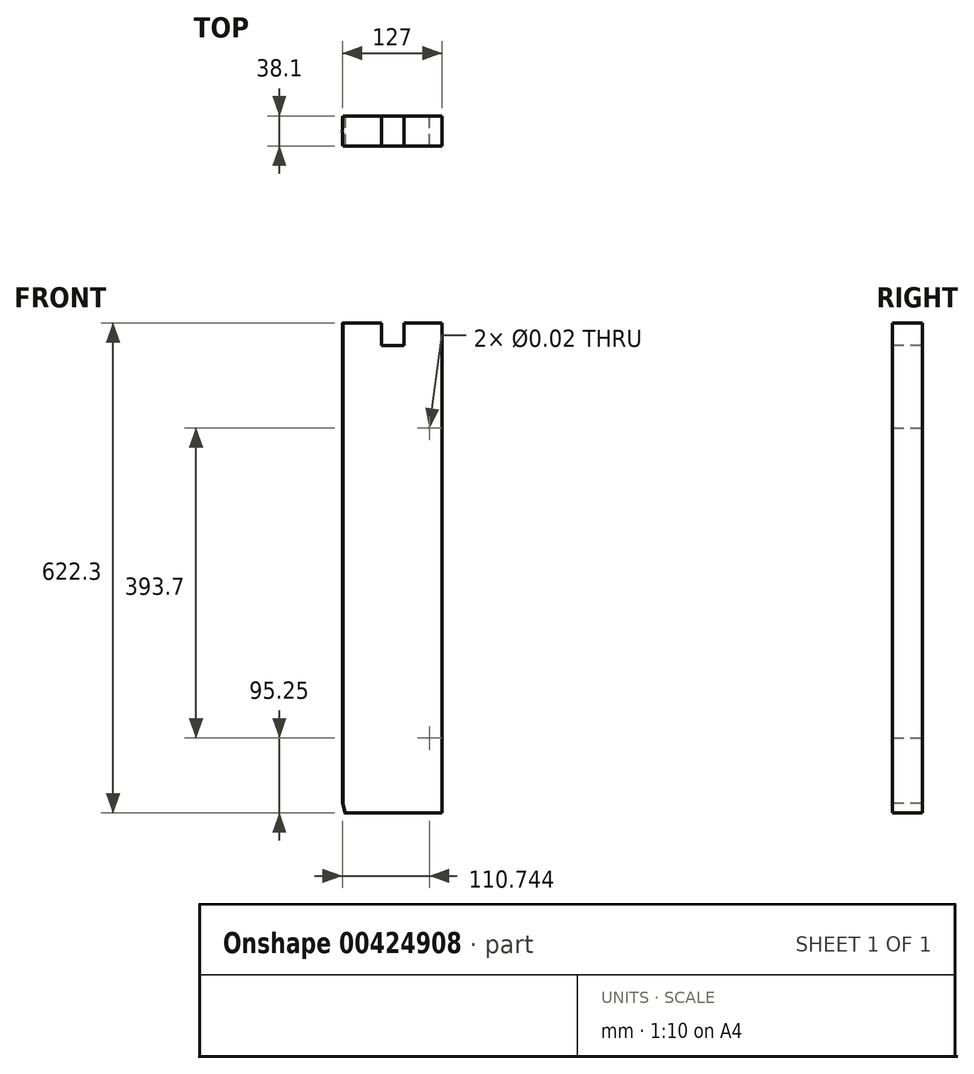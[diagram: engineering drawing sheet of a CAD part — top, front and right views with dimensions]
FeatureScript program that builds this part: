
annotation { "Feature Type Name" : "Feature", "Feature Type Description" : "" }
export const myFeature = defineFeature(function(context is Context, id is Id, definition is map)
    precondition{}
    {
        {
            var Q0;
            Q0=qCreatedBy(makeId("Front.planeOp"),FACE);
            var sketch = newSketch(context, id + "F0", { "sketchPlane" : qUnion([Q0])});
            skLineSegment(sketch, "E0.bottom", {"start": v(63.5, -311.15) * mm, "end": v(-63.5, -311.15) * mm});
            skLineSegment(sketch, "E0.top", {"start": v(63.5, 311.15) * mm, "end": v(-63.5, 311.15) * mm});
            skLineSegment(sketch, "E0.left", {"start": v(63.5, -311.15) * mm, "end": v(63.5, 311.15) * mm});
            skLineSegment(sketch, "E0.right", {"start": v(-63.5, -311.15) * mm, "end": v(-63.5, 311.15) * mm});
            skPoint(sketch, "E0.middle", {"position": v(0, 0) * mm});
            skSolve(sketch);
        }
        {
            var Q0;
            Q0 = qSketchRegion(id + "F0", true);
            extrude(context, id + "F1", {"entities" : qUnion([Q0]), "depth" : 38.1 * mm, "symmetric" : true});
        }
        {
            var Q0;
            Q0=makeQuery(id+"F1.opExtrude","SWEPT_FACE",FACE,{"disambiguationData":[OSD([sQuery(id+"F0.wireOp",EDGE,"E0.top")])]});
            var sketch = newSketch(context, id + "F2", { "sketchPlane" : qUnion([Q0])});
            skLineSegment(sketch, "E1", {"start": v(-63.5, 0) * mm, "end": v(63.5, 0) * mm, "construction": true});
            skCircle(sketch, "E2", {"center": v(186.47, 0) * mm, "radius": 249.97 * mm});
            skLineSegment(sketch, "E3.0", {"start": v(63.5, -19.05) * mm, "end": v(-63.5, -19.05) * mm});
            skLineSegment(sketch, "E4.0", {"start": v(-63.5, -19.05) * mm, "end": v(-63.5, 19.05) * mm});
            skLineSegment(sketch, "E5.0", {"start": v(63.5, 19.05) * mm, "end": v(-63.5, 19.05) * mm});
            skSolve(sketch);
        }
        {
            var Q0;
            {var subQ0=sQuery(id+"F2.wireOp",EDGE,"E4.0");var subQ1=sQuery(id+"F2.wireOp",EDGE,"E2");var subQ2=makeQuery(id+"F2.imprint","INTERSECT",VERTEX,{"derivedFrom":[subQ1,subQ0]});Q0=makeQuery(id+"F2.imprint","IMPRINT",FACE,{"disambiguationData":[TD([[makeQuery(id+"F2.imprint","IMPRINT",EDGE,{"disambiguationData":[TD([[subQ2,1.0]])],"derivedFrom":subQ1}),-1.0]])]});}
            var Q1;
            {var subQ0=sQuery(id+"F2.wireOp",EDGE,"E4.0");var subQ1=sQuery(id+"F2.wireOp",EDGE,"E2");var subQ2=makeQuery(id+"F2.imprint","INTERSECT",VERTEX,{"derivedFrom":[subQ1,subQ0]});Q1=makeQuery(id+"F2.imprint","IMPRINT",FACE,{"disambiguationData":[TD([[makeQuery(id+"F2.imprint","IMPRINT",EDGE,{"disambiguationData":[TD([[subQ2,-1.0]])],"derivedFrom":subQ1}),-1.0]])]});}
            extrude(context, id + "F3", {"entities" : qUnion([Q0, Q1]), "operationType" : NewBodyOperationType.REMOVE, "endBound" : BoundingType.THROUGH_ALL, "oppositeDirection" : true, "depth" : 25.4 * mm});
        }
        {
            var Q0;
            Q0=makeQuery(id+"F1.opExtrude","CAP_FACE",FACE,{"disambiguationData":[OSD([sQuery(id+"F0.wireOp",EDGE,"E0.bottom"),sQuery(id+"F0.wireOp",EDGE,"E0.top"),sQuery(id+"F0.wireOp",EDGE,"E0.left"),sQuery(id+"F0.wireOp",EDGE,"E0.right")])],"isStart":false});
            var sketch = newSketch(context, id + "F4", { "sketchPlane" : qUnion([Q0])});
            skLineSegment(sketch, "E6", {"start": v(47.24, 311.15) * mm, "end": v(47.24, -311.15) * mm, "construction": true});
            skPoint(sketch, "E7", {"position": v(47.24, -215.9) * mm});
            skPoint(sketch, "E8", {"position": v(47.24, 177.8) * mm});
            skSolve(sketch);
        }
        {
            var Q0;
            Q0=sQuery(id+"F4.wireOp",VERTEX,"E8");
            var Q1;
            Q1=sQuery(id+"F4.wireOp",VERTEX,"E7");
            var Q2;
            Q2=makeQuery(id+"F1.opExtrude","SWEPT_BODY",BODY,{"disambiguationData":[OSD([sQuery(id+"F0.wireOp",EDGE,"E0.bottom"),sQuery(id+"F0.wireOp",EDGE,"E0.top"),sQuery(id+"F0.wireOp",EDGE,"E0.left"),sQuery(id+"F0.wireOp",EDGE,"E0.right")])]});
            hole(context, id + "F5", {"style" : HoleStyle.SIMPLE, "endStyle" : HoleEndStyle.THROUGH, "standardTappedOrClearance" : lookupTablePath({ "standard" : "ANSI", "size" : "1/2 (0.5)", "type" : "Drilled" }), "standardBlindInLast" : lookupTablePath({ "standard" : "ANSI", "size" : "1/2", "type" : "Drilled" }), "holeDiameter" : 1 / 50.8 * mm, "isTappedThrough" : true, "tappedDepth" : 10.3 * mm, "tapClearance" : 3, "locations" : qUnion([Q0, Q1]), "scope" : qUnion([Q2]), "startStyle" : HoleStartStyle.SKETCH});
        }
        {
            var Q0;
            Q0=makeQuery(id+"F1.opExtrude","CAP_FACE",FACE,{"disambiguationData":[OSD([sQuery(id+"F0.wireOp",EDGE,"E0.bottom"),sQuery(id+"F0.wireOp",EDGE,"E0.top"),sQuery(id+"F0.wireOp",EDGE,"E0.left"),sQuery(id+"F0.wireOp",EDGE,"E0.right")])],"isStart":false});
            var sketch = newSketch(context, id + "F6", { "sketchPlane" : qUnion([Q0])});
            skLineSegment(sketch, "E9", {"start": v(63.5, 0) * mm, "end": v(-62.77, 0) * mm, "construction": true});
            skLineSegment(sketch, "E10.bottom", {"start": v(-13.56, 311.15) * mm, "end": v(15.01, 311.15) * mm});
            skLineSegment(sketch, "E10.top", {"start": v(-13.56, 282.58) * mm, "end": v(15.01, 282.58) * mm});
            skLineSegment(sketch, "E10.left", {"start": v(-13.56, 311.15) * mm, "end": v(-13.56, 282.58) * mm});
            skLineSegment(sketch, "E10.right", {"start": v(15.01, 311.15) * mm, "end": v(15.01, 282.58) * mm});
            skSolve(sketch);
        }
        {
            var Q0;
            Q0 = qSketchRegion(id + "F6", true);
            extrude(context, id + "F7", {"entities" : qUnion([Q0]), "operationType" : NewBodyOperationType.REMOVE, "endBound" : BoundingType.THROUGH_ALL, "oppositeDirection" : true, "depth" : 25.4 * mm});
        }
        {
            var Q0;
            {var subQ0=sQuery(id+"F2.wireOp",EDGE,"E2");var subQ1=makeQuery(id+"F2.imprint","INTERSECT",VERTEX,{"derivedFrom":[subQ0,sQuery(id+"F2.wireOp",EDGE,"E4.0")]});Q0=makeQuery(id+"F3.boolean.opBoolean","TWEAK_EDGE",EDGE,{"derivedFrom":[makeQuery(id+"F3.opExtrude","CAP_EDGE",EDGE,{"disambiguationData":[OSD([subQ0]),TDD([makeQuery(id+"F2.imprint","IMPRINT",EDGE,{"disambiguationData":[TD([[subQ1,1.0]])],"derivedFrom":subQ0})])],"isStart":true}),makeQuery(id+"F3.opExtrude","CAP_EDGE",EDGE,{"disambiguationData":[OSD([subQ0]),TDD([makeQuery(id+"F2.imprint","IMPRINT",EDGE,{"disambiguationData":[TD([[subQ1,-1.0]])],"derivedFrom":subQ0})])],"isStart":true})]});}
            var Q1;
            {var subQ0=sQuery(id+"F2.wireOp",EDGE,"E2");var subQ1=makeQuery(id+"F2.imprint","INTERSECT",VERTEX,{"derivedFrom":[subQ0,sQuery(id+"F2.wireOp",EDGE,"E4.0")]});Q1=makeQuery(id+"F3.boolean.opBoolean","INTERSECT",EDGE,{"derivedFrom":[makeQuery(id+"F1.opExtrude","SWEPT_FACE",FACE,{"disambiguationData":[OSD([sQuery(id+"F0.wireOp",EDGE,"E0.bottom")])]}),makeQuery(id+"F3.opExtrude","SWEPT_FACE",FACE,{"disambiguationData":[OSD([subQ0]),TDD([makeQuery(id+"F2.imprint","IMPRINT",EDGE,{"disambiguationData":[TD([[subQ1,1.0]])],"derivedFrom":subQ0})])]}),makeQuery(id+"F3.opExtrude","SWEPT_FACE",FACE,{"disambiguationData":[OSD([subQ0]),TDD([makeQuery(id+"F2.imprint","IMPRINT",EDGE,{"disambiguationData":[TD([[subQ1,-1.0]])],"derivedFrom":subQ0})])]})]});}
            chamfer(context, id + "F8", {"entities" : qUnion([Q0, Q1]), "chamferType" : ChamferType.TWO_OFFSETS, "width1" : 12.7 * mm, "oppositeDirection" : true, "width2" : 3.17 * mm, "tangentPropagation" : true});
        }
    });
